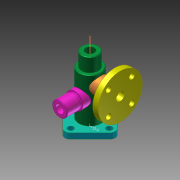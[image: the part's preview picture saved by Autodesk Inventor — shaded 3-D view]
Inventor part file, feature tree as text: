
AUTODESK INVENTOR PART (.ipt)
format: ipt  version: 2011 SP2 (Build 150309200, 309)  size: 270,336 bytes
history: native  units: mm
features: sketch x9, extrude x8, hole x4, plane x2, revolve x2, chamfer x1, projected_geometry x1
ambient origin geometry x8: Origin, YZ Plane, XZ Plane, XY Plane, X Axis, Y Axis, Z Axis, Center Point
bodies: Solid1 (feature_tree), Solid2 (feature_tree), Solid3 (feature_tree), Solid4 (feature_tree), Solid5 (feature_tree), Solid6 (feature_tree), Solid7 (feature_tree), Solid8 (feature_tree)
feature tree (27):
  extrude  "Extrusion1"  Depth=10.0mm
  extrude  "Extrusion2"  Depth=10.0mm
  extrude  "Extrusion3"  Depth=5.0mm
  plane  "Work Plane1"
  extrude  "Extrusion4"  Depth=40.0mm TaperAngle=360.0deg
  extrude  "Extrusion5"  Depth=20.0mm
  extrude  "Extrusion6"  Depth=15.0mm
  plane  "Work Plane2"
  extrude  "Extrusion7"  [1 undecoded]
  extrude  "Extrusion8"  Depth=50.0mm
  hole  "Hole3"  [1 undecoded]
  hole  "Hole4"  [1 undecoded]
  sketch  "Sketch10"  dims[d22=24.0mm d23=0.0mm d24=13.0mm d25=3.0mm d26=0.0mm d27=15.0mm d28=3.0mm d29=0.0mm d30=55.0mm d31=40.0mm d32=70.0mm d33=5.0mm d34=30.0mm d35=45.0deg d36=40.0mm d38=360.0deg d40=10.0mm d41=0.0mm d42=15.0mm d43=10.0mm d44=0.0mm d63=10.0mm d64=10.0mm d65=16.0mm d66=6.0mm d67=4.0mm d68=2.0mm d69=90.0deg d70=30.0mm d71=0.0mm d72=10.0mm d73=10.0mm d74=25.0mm d75=6.0mm d76=4.0mm d77=2.0mm d78=90.0deg d79=50.0mm d80=0.0mm d82=15.0mm d83=90.0deg d84=90.0deg d85=10.0mm d86=10.0mm d87=15.0mm d88=6.0mm d89=4.0mm d90=2.0mm d91=90.0deg d92=55.0mm d93=0.0mm d94=10.0mm d95=10.0mm d96=15.0mm d97=6.0mm d98=4.0mm d99=2.0mm d100=90.0deg d101=55.0mm d102=0.0mm d103=1.0mm d104=2.0mm d105=45.0deg]
  revolve  "Revolution1"  [1 undecoded]
  revolve  "Revolution2"  [1 undecoded]
  hole  "Hole5"  [1 undecoded]
  hole  "Hole6"  [1 undecoded]
  chamfer  "Chamfer1"  Distance=70.0mm
  sketch  "Sketch1"  dims[d0=70.0mm d1=10.0mm]
  sketch  "Sketch2"  dims[d2=10.0mm d3=10.0mm]
  sketch  "Sketch3"  dims[d4=10.0mm d5=5.0mm]
  sketch  "Sketch4"  dims[d6=35.0mm d7=40.0mm d9=360.0deg]
  sketch  "Sketch5"  dims[d11=10.0mm d12=0.0mm d13=20.0mm]
  sketch  "Sketch6"  dims[d14=80.0mm d15=0.0mm d16=15.0mm]
  sketch  "Sketch7"  dims[d17=25.0mm d18=0.0mm d19=-55.0mm]
  sketch  "Sketch8"  dims[d20=13.5mm d21=50.0mm]
  projected_geometry  "Projected Loop1"
note: 7 required parameter values undecoded (feature->parameter linkage not recoverable at this tier; creation-order binding heuristic only, values carry confidence <= 0.55)